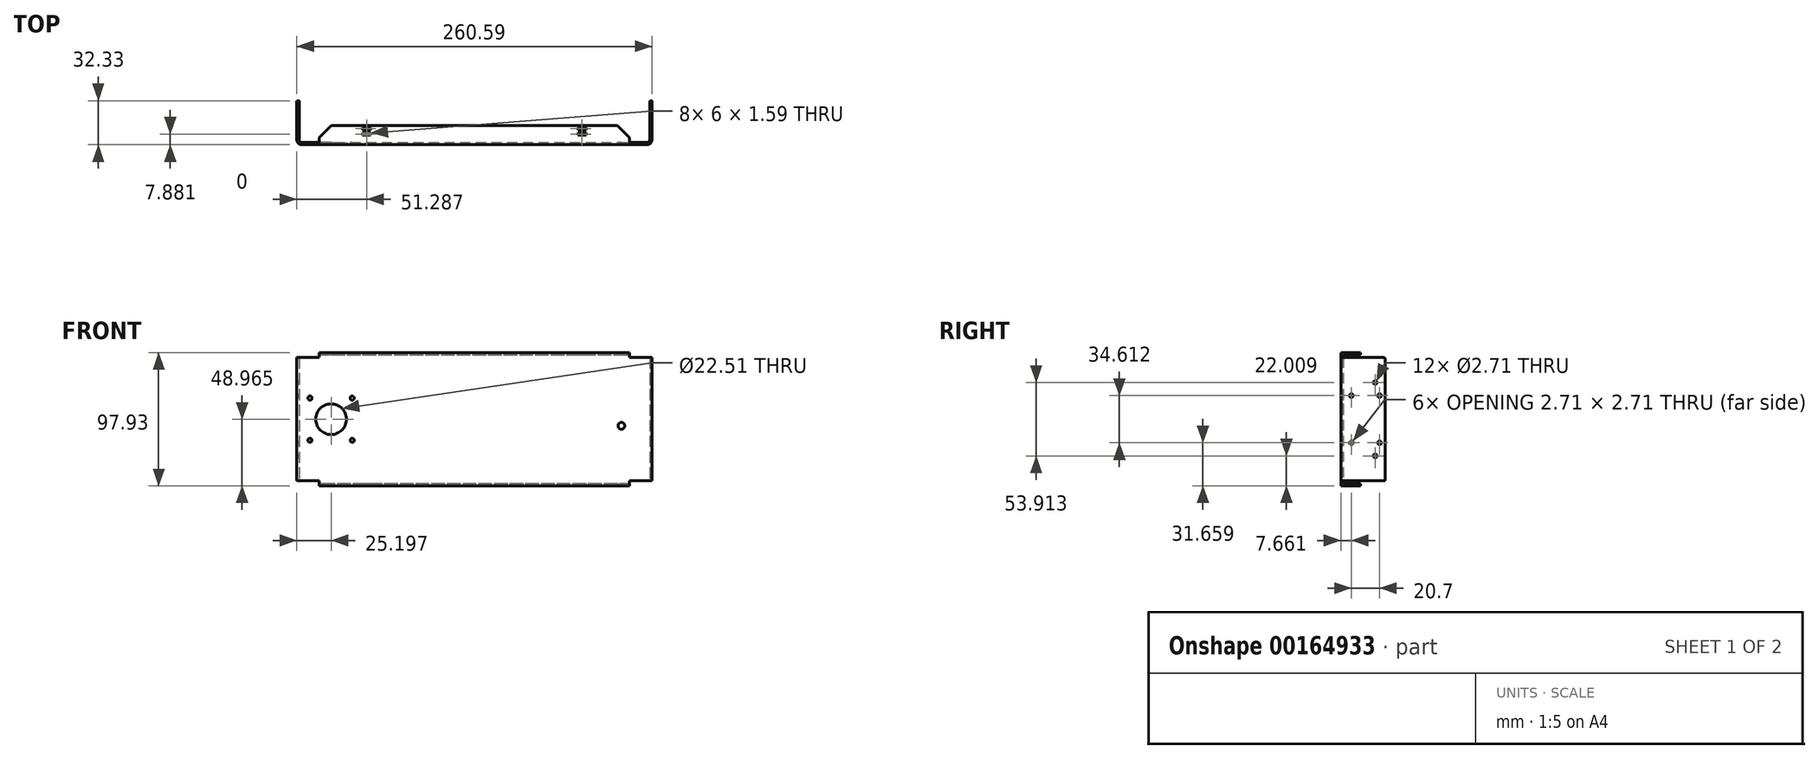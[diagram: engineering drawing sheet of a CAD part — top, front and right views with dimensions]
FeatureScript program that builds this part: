
annotation { "Feature Type Name" : "Feature", "Feature Type Description" : "" }
export const myFeature = defineFeature(function(context is Context, id is Id, definition is map)
    precondition{}
    {
        {
            var Q0;
            Q0=qCreatedBy(makeId("Top.planeOp"),FACE);
            var sketch = newSketch(context, id + "F0", { "sketchPlane" : qUnion([Q0])});
            skLineSegment(sketch, "E0", {"start": v(0, 0) * mm, "end": v(0, -30.62) * mm});
            skLineSegment(sketch, "E1", {"start": v(-1.7, -32.33) * mm, "end": v(-1.7, 0) * mm});
            skLineSegment(sketch, "E2", {"start": v(257.18, -30.62) * mm, "end": v(257.18, 0) * mm});
            skLineSegment(sketch, "E3", {"start": v(258.88, 0) * mm, "end": v(258.88, -32.33) * mm});
            skLineSegment(sketch, "E4", {"start": v(-1.7, -32.33) * mm, "end": v(258.88, -32.33) * mm});
            skLineSegment(sketch, "E5", {"start": v(0, -30.62) * mm, "end": v(257.18, -30.62) * mm});
            skLineSegment(sketch, "E6", {"start": v(257.18, 0) * mm, "end": v(258.88, 0) * mm});
            skLineSegment(sketch, "E7", {"start": v(0, 0) * mm, "end": v(-1.7, 0) * mm});
            skLineSegment(sketch, "E8", {"start": v(128.59, -30.62) * mm, "end": v(128.59, -32.33) * mm, "construction": true});
            skLineSegment(sketch, "E9", {"start": v(258.88, 0) * mm, "end": v(257.18, 0) * mm, "construction": true});
            skSolve(sketch);
        }
        {
            var Q0;
            Q0=qSketchRegion(id+"F0",true);
            extrude(context, id + "F1", {"entities" : qUnion([Q0]), "depth" : 90.55 * mm});
        }
        {
            var Q0;
            Q0=makeQuery(id+"F1.opExtrude","SWEPT_FACE",FACE,{"disambiguationData":[OSD([sQuery(id+"F0.wireOp",EDGE,"E4")])]});
            var sketch = newSketch(context, id + "F2", { "sketchPlane" : qUnion([Q0])});
            skLineSegment(sketch, "E10.bottom", {"start": v(38.99, 60.77) * mm, "end": v(7.99, 60.77) * mm, "construction": true});
            skLineSegment(sketch, "E10.top", {"start": v(38.99, 29.78) * mm, "end": v(7.99, 29.78) * mm, "construction": true});
            skLineSegment(sketch, "E10.left", {"start": v(38.99, 60.77) * mm, "end": v(38.99, 29.78) * mm, "construction": true});
            skLineSegment(sketch, "E10.right", {"start": v(7.99, 60.77) * mm, "end": v(7.99, 29.78) * mm, "construction": true});
            skPoint(sketch, "E10.middle", {"position": v(23.49, 45.28) * mm});
            skCircle(sketch, "E11", {"center": v(23.49, 45.28) * mm, "radius": 11.25 * mm});
            skCircle(sketch, "E12", {"center": v(7.99, 29.78) * mm, "radius": 1.5 * mm});
            skCircle(sketch, "E13", {"center": v(38.99, 29.78) * mm, "radius": 1.5 * mm});
            skCircle(sketch, "E14", {"center": v(38.99, 60.77) * mm, "radius": 1.5 * mm});
            skCircle(sketch, "E15", {"center": v(7.99, 60.77) * mm, "radius": 1.5 * mm});
            skLineSegment(sketch, "E16", {"start": v(23.49, 45.28) * mm, "end": v(-1.7, 45.28) * mm, "construction": true});
            skLineSegment(sketch, "E17", {"start": v(23.49, 45.28) * mm, "end": v(236.47, 45.28) * mm, "construction": true});
            skLineSegment(sketch, "E18", {"start": v(236.47, 40.45) * mm, "end": v(236.47, 45.28) * mm, "construction": true});
            skCircle(sketch, "E19", {"center": v(236.47, 40.45) * mm, "radius": 2.5 * mm});
            skLineSegment(sketch, "E20", {"start": v(236.47, 40.45) * mm, "end": v(258.88, 40.45) * mm, "construction": true});
            skSolve(sketch);
        }
        {
            var Q0;
            Q0 = qSketchRegion(id + "F2", true);
            var Q1;
            Q1=makeQuery(id+"F1.opExtrude","SWEPT_FACE",FACE,{"disambiguationData":[OSD([sQuery(id+"F0.wireOp",EDGE,"E5")])]});
            extrude(context, id + "F3", {"entities" : qUnion([Q0]), "operationType" : NewBodyOperationType.REMOVE, "endBound" : BoundingType.UP_TO_SURFACE, "oppositeDirection" : true, "endBoundEntityFace" : qUnion([Q1]), "depth" : 25.4 * mm});
        }
        {
            var Q0;
            Q0=makeQuery(id+"F1.opExtrude","SWEPT_FACE",FACE,{"disambiguationData":[OSD([sQuery(id+"F0.wireOp",EDGE,"E3")])]});
            var sketch = newSketch(context, id + "F4", { "sketchPlane" : qUnion([Q0])});
            skLineSegment(sketch, "E21", {"start": v(0, 45.28) * mm, "end": v(-7.17, 45.28) * mm, "construction": true});
            skLineSegment(sketch, "E22", {"start": v(-7.17, 18.32) * mm, "end": v(-7.17, 72.23) * mm, "construction": true});
            skCircle(sketch, "E23", {"center": v(-7.17, 18.32) * mm, "radius": 1.35 * mm});
            skCircle(sketch, "E24", {"center": v(-7.17, 72.23) * mm, "radius": 1.35 * mm});
            skLineSegment(sketch, "E25", {"start": v(-7.17, 72.23) * mm, "end": v(-7.17, 90.55) * mm, "construction": true});
            skSolve(sketch);
        }
        {
            var Q0;
            Q0 = qSketchRegion(id + "F4", true);
            var Q1;
            Q1=makeQuery(id+"F1.opExtrude","SWEPT_FACE",FACE,{"disambiguationData":[OSD([sQuery(id+"F0.wireOp",EDGE,"E1")])]});
            extrude(context, id + "F5", {"entities" : qUnion([Q0]), "operationType" : NewBodyOperationType.REMOVE, "endBound" : BoundingType.UP_TO_SURFACE, "oppositeDirection" : true, "endBoundEntityFace" : qUnion([Q1]), "depth" : 25.4 * mm});
        }
        {
            var Q0;
            Q0=makeQuery(id+"F1.opExtrude","CAP_EDGE",EDGE,{"disambiguationData":[OSD([sQuery(id+"F0.wireOp",EDGE,"E6")])],"isStart":false});
            var Q1;
            Q1=makeQuery(id+"F1.opExtrude","CAP_EDGE",EDGE,{"disambiguationData":[OSD([sQuery(id+"F0.wireOp",EDGE,"E6")])],"isStart":true});
            var Q2;
            Q2=makeQuery(id+"F1.opExtrude","CAP_EDGE",EDGE,{"disambiguationData":[OSD([sQuery(id+"F0.wireOp",EDGE,"E7")])],"isStart":false});
            var Q3;
            Q3=makeQuery(id+"F1.opExtrude","CAP_EDGE",EDGE,{"disambiguationData":[OSD([sQuery(id+"F0.wireOp",EDGE,"E7")])],"isStart":true});
            fillet(context, id + "F6", {"entities" : qUnion([Q0, Q1, Q2, Q3]), "radius" : 0.76 * mm, "tangentPropagation" : true, "allowEdgeOverflow" : false});
        }
        {
            var Q0;
            Q0=makeQuery(id+"F1.opExtrude","SWEPT_FACE",FACE,{"disambiguationData":[OSD([sQuery(id+"F0.wireOp",EDGE,"E3")])]});
            var sketch = newSketch(context, id + "F7", { "sketchPlane" : qUnion([Q0])});
            skLineSegment(sketch, "E26", {"start": v(-28.64, 45.28) * mm, "end": v(0, 45.28) * mm, "construction": true});
            skLineSegment(sketch, "E27.bottom", {"start": v(-24.67, 62.58) * mm, "end": v(-3.97, 62.58) * mm, "construction": true});
            skLineSegment(sketch, "E27.top", {"start": v(-24.67, 27.97) * mm, "end": v(-3.97, 27.97) * mm, "construction": true});
            skLineSegment(sketch, "E27.left", {"start": v(-24.67, 62.58) * mm, "end": v(-24.67, 27.97) * mm, "construction": true});
            skLineSegment(sketch, "E27.right", {"start": v(-3.97, 62.58) * mm, "end": v(-3.97, 27.97) * mm, "construction": true});
            skPoint(sketch, "E27.middle", {"position": v(-14.32, 45.28) * mm});
            skLineSegment(sketch, "E28", {"start": v(-24.67, 27.97) * mm, "end": v(-24.67, 0) * mm, "construction": true});
            skLineSegment(sketch, "E29", {"start": v(-24.67, 27.97) * mm, "end": v(-28.64, 27.97) * mm, "construction": true});
            skCircle(sketch, "E30", {"center": v(-24.67, 27.97) * mm, "radius": 1.35 * mm});
            skCircle(sketch, "E31", {"center": v(-3.97, 27.97) * mm, "radius": 1.35 * mm});
            skCircle(sketch, "E32", {"center": v(-3.97, 62.58) * mm, "radius": 1.35 * mm});
            skCircle(sketch, "E33", {"center": v(-24.67, 62.58) * mm, "radius": 1.35 * mm});
            skLineSegment(sketch, "E34", {"start": v(-28.64, 0) * mm, "end": v(-28.64, 90.55) * mm, "construction": true});
            skSolve(sketch);
        }
        {
            var Q0;
            Q0 = qSketchRegion(id + "F7", true);
            var Q1;
            Q1=makeQuery(id+"F1.opExtrude","SWEPT_FACE",FACE,{"disambiguationData":[OSD([sQuery(id+"F0.wireOp",EDGE,"E1")])]});
            extrude(context, id + "F8", {"entities" : qUnion([Q0]), "operationType" : NewBodyOperationType.REMOVE, "endBound" : BoundingType.UP_TO_SURFACE, "oppositeDirection" : true, "endBoundEntityFace" : qUnion([Q1]), "depth" : 25.4 * mm});
        }
        {
            var Q0;
            Q0=makeQuery(id+"F1.opExtrude","SWEPT_FACE",FACE,{"disambiguationData":[OSD([sQuery(id+"F0.wireOp",EDGE,"E5")])]});
            var sketch = newSketch(context, id + "F9", { "sketchPlane" : qUnion([Q0])});
            skLineSegment(sketch, "E35.bottom", {"start": v(-14.68, 0) * mm, "end": v(-242.5, 0) * mm});
            skLineSegment(sketch, "E35.top", {"start": v(-14.68, -3.7) * mm, "end": v(-242.5, -3.7) * mm});
            skLineSegment(sketch, "E35.left", {"start": v(-14.68, 0) * mm, "end": v(-14.68, -3.7) * mm});
            skLineSegment(sketch, "E35.right", {"start": v(-242.5, 0) * mm, "end": v(-242.5, -3.7) * mm});
            skPoint(sketch, "E36", {"position": v(-128.59, 0) * mm});
            skLineSegment(sketch, "E37.bottom", {"start": v(-14.68, 90.55) * mm, "end": v(-242.5, 90.55) * mm});
            skLineSegment(sketch, "E37.top", {"start": v(-14.68, 94.24) * mm, "end": v(-242.5, 94.24) * mm});
            skLineSegment(sketch, "E37.left", {"start": v(-14.68, 90.55) * mm, "end": v(-14.68, 94.24) * mm});
            skLineSegment(sketch, "E37.right", {"start": v(-242.5, 90.55) * mm, "end": v(-242.5, 94.24) * mm});
            skSolve(sketch);
        }
        {
            var Q0;
            Q0 = qSketchRegion(id + "F9", true);
            var Q1;
            Q1=makeQuery(id+"F1.opExtrude","SWEPT_FACE",FACE,{"disambiguationData":[OSD([sQuery(id+"F0.wireOp",EDGE,"E4")])]});
            extrude(context, id + "F10", {"entities" : qUnion([Q0]), "operationType" : NewBodyOperationType.ADD, "endBound" : BoundingType.UP_TO_SURFACE, "oppositeDirection" : true, "endBoundEntityFace" : qUnion([Q1]), "depth" : 25.4 * mm});
        }
        {
            var Q0;
            Q0=makeQuery(id+"F10.boolean.opBoolean","MERGE",FACE,{"derivedFrom":[makeQuery(id+"F1.opExtrude","SWEPT_FACE",FACE,{"disambiguationData":[OSD([sQuery(id+"F0.wireOp",EDGE,"E5")])]}),makeQuery(id+"F10.opExtrude","CAP_FACE",FACE,{"disambiguationData":[OSD([sQuery(id+"F9.wireOp",EDGE,"E35.bottom"),sQuery(id+"F9.wireOp",EDGE,"E35.top"),sQuery(id+"F9.wireOp",EDGE,"E35.left"),sQuery(id+"F9.wireOp",EDGE,"E35.right")])],"isStart":true}),makeQuery(id+"F10.opExtrude","CAP_FACE",FACE,{"disambiguationData":[OSD([sQuery(id+"F9.wireOp",EDGE,"E37.bottom"),sQuery(id+"F9.wireOp",EDGE,"E37.top"),sQuery(id+"F9.wireOp",EDGE,"E37.left"),sQuery(id+"F9.wireOp",EDGE,"E37.right")])],"isStart":true})]});
            var sketch = newSketch(context, id + "F11", { "sketchPlane" : qUnion([Q0])});
            skLineSegment(sketch, "E38.bottom", {"start": v(-14.68, 94.24) * mm, "end": v(-242.5, 94.24) * mm});
            skLineSegment(sketch, "E38.top", {"start": v(-14.68, 92.53) * mm, "end": v(-242.5, 92.53) * mm});
            skLineSegment(sketch, "E38.left", {"start": v(-14.68, 94.24) * mm, "end": v(-14.68, 92.53) * mm});
            skLineSegment(sketch, "E38.right", {"start": v(-242.5, 94.24) * mm, "end": v(-242.5, 92.53) * mm});
            skLineSegment(sketch, "E39.bottom", {"start": v(-242.5, -3.7) * mm, "end": v(-14.68, -3.7) * mm});
            skLineSegment(sketch, "E39.top", {"start": v(-242.5, -1.98) * mm, "end": v(-14.68, -1.98) * mm});
            skLineSegment(sketch, "E39.left", {"start": v(-242.5, -3.7) * mm, "end": v(-242.5, -1.98) * mm});
            skLineSegment(sketch, "E39.right", {"start": v(-14.68, -3.7) * mm, "end": v(-14.68, -1.98) * mm});
            skSolve(sketch);
        }
        {
            var Q0;
            Q0 = qSketchRegion(id + "F11", true);
            extrude(context, id + "F12", {"entities" : qUnion([Q0]), "operationType" : NewBodyOperationType.ADD, "depth" : 12.52 * mm});
        }
        {
            var Q0;
            Q0=makeQuery(id+"F1.opExtrude","SWEPT_EDGE",EDGE,{"disambiguationData":[OSD([sQuery(id+"F0.wireOp",EDGE,"E1"),sQuery(id+"F0.wireOp",EDGE,"E4")])]});
            var Q1;
            Q1=makeQuery(id+"F1.opExtrude","SWEPT_EDGE",EDGE,{"disambiguationData":[OSD([sQuery(id+"F0.wireOp",EDGE,"E3"),sQuery(id+"F0.wireOp",EDGE,"E4")])]});
            var Q2;
            Q2=makeQuery(id+"F10.opExtrude","TWEAK_EDGE",EDGE,{"derivedFrom":[makeQuery(id+"F1.opExtrude","SWEPT_FACE",FACE,{"disambiguationData":[OSD([sQuery(id+"F0.wireOp",EDGE,"E4")])]}),makeQuery(id+"F9.imprint","IMPRINT",EDGE,{"derivedFrom":sQuery(id+"F9.wireOp",EDGE,"E37.top")})]});
            var Q3;
            Q3=makeQuery(id+"F10.opExtrude","TWEAK_EDGE",EDGE,{"derivedFrom":[makeQuery(id+"F1.opExtrude","SWEPT_FACE",FACE,{"disambiguationData":[OSD([sQuery(id+"F0.wireOp",EDGE,"E4")])]}),makeQuery(id+"F9.imprint","IMPRINT",EDGE,{"derivedFrom":sQuery(id+"F9.wireOp",EDGE,"E35.top")})]});
            fillet(context, id + "F13", {"entities" : qUnion([Q0, Q1, Q2, Q3]), "radius" : 3.7 * mm, "tangentPropagation" : true, "allowEdgeOverflow" : false});
        }
        {
            var Q0;
            Q0=makeQuery(id+"F1.opExtrude","SWEPT_EDGE",EDGE,{"disambiguationData":[OSD([sQuery(id+"F0.wireOp",EDGE,"E0"),sQuery(id+"F0.wireOp",EDGE,"E5")])]});
            var Q1;
            Q1=makeQuery(id+"F1.opExtrude","SWEPT_EDGE",EDGE,{"disambiguationData":[OSD([sQuery(id+"F0.wireOp",EDGE,"E2"),sQuery(id+"F0.wireOp",EDGE,"E5")])]});
            var Q2;
            Q2=makeQuery(id+"F12.opExtrude","CAP_EDGE",EDGE,{"disambiguationData":[OSD([sQuery(id+"F11.wireOp",EDGE,"E38.top")])],"isStart":true});
            var Q3;
            Q3=makeQuery(id+"F12.opExtrude","CAP_EDGE",EDGE,{"disambiguationData":[OSD([sQuery(id+"F11.wireOp",EDGE,"E39.top")])],"isStart":true});
            fillet(context, id + "F14", {"entities" : qUnion([Q0, Q1, Q2, Q3]), "radius" : 1.98 * mm, "tangentPropagation" : true, "allowEdgeOverflow" : false});
        }
        {
            var Q0;
            Q0=makeQuery(id+"F12.opExtrude","CAP_EDGE",EDGE,{"disambiguationData":[OSD([sQuery(id+"F11.wireOp",EDGE,"E38.left")])],"isStart":false});
            var Q1;
            Q1=makeQuery(id+"F12.opExtrude","CAP_EDGE",EDGE,{"disambiguationData":[OSD([sQuery(id+"F11.wireOp",EDGE,"E38.right")])],"isStart":false});
            var Q2;
            Q2=makeQuery(id+"F12.opExtrude","CAP_EDGE",EDGE,{"disambiguationData":[OSD([sQuery(id+"F11.wireOp",EDGE,"E39.left")])],"isStart":false});
            var Q3;
            Q3=makeQuery(id+"F12.opExtrude","CAP_EDGE",EDGE,{"disambiguationData":[OSD([sQuery(id+"F11.wireOp",EDGE,"E39.right")])],"isStart":false});
            chamfer(context, id + "F15", {"entities" : qUnion([Q0, Q1, Q2, Q3]), "width" : 8.95 * mm, "tangentPropagation" : true});
        }
        {
            var Q0;
            Q0=makeQuery(id+"F12.boolean.opBoolean","MERGE",FACE,{"derivedFrom":[makeQuery(id+"F10.opExtrude","SWEPT_FACE",FACE,{"disambiguationData":[OSD([sQuery(id+"F9.wireOp",EDGE,"E35.top")])]}),makeQuery(id+"F12.opExtrude","SWEPT_FACE",FACE,{"disambiguationData":[OSD([sQuery(id+"F11.wireOp",EDGE,"E39.bottom")])]})]});
            var sketch = newSketch(context, id + "F16", { "sketchPlane" : qUnion([Q0])});
            skLineSegment(sketch, "E40", {"start": v(23.49, 32.33) * mm, "end": v(23.49, 20.48) * mm, "construction": true});
            skLineSegment(sketch, "E41", {"start": v(23.49, 20.48) * mm, "end": v(46.58, 20.48) * mm, "construction": true});
            skLineSegment(sketch, "E42.bottom", {"start": v(46.58, 21.27) * mm, "end": v(52.58, 21.27) * mm});
            skLineSegment(sketch, "E42.top", {"start": v(46.58, 19.69) * mm, "end": v(52.58, 19.69) * mm});
            skLineSegment(sketch, "E42.left", {"start": v(46.58, 21.27) * mm, "end": v(46.58, 19.69) * mm});
            skLineSegment(sketch, "E42.right", {"start": v(52.58, 21.27) * mm, "end": v(52.58, 19.69) * mm});
            skLineSegment(sketch, "E43", {"start": v(49.58, 19.69) * mm, "end": v(49.58, 18.1) * mm, "construction": true});
            skLineSegment(sketch, "E44.bottom", {"start": v(204.6, 21.27) * mm, "end": v(210.6, 21.27) * mm});
            skLineSegment(sketch, "E44.top", {"start": v(204.6, 19.69) * mm, "end": v(210.6, 19.69) * mm});
            skLineSegment(sketch, "E44.left", {"start": v(204.6, 21.27) * mm, "end": v(204.6, 19.69) * mm});
            skLineSegment(sketch, "E44.right", {"start": v(210.6, 21.27) * mm, "end": v(210.6, 19.69) * mm});
            skLineSegment(sketch, "E45", {"start": v(52.58, 20.48) * mm, "end": v(204.6, 20.48) * mm, "construction": true});
            skLineSegment(sketch, "E46", {"start": v(128.59, 20.48) * mm, "end": v(128.59, 18.1) * mm, "construction": true});
            skLineSegment(sketch, "E47", {"start": v(207.6, 21.27) * mm, "end": v(207.6, 23.66) * mm, "construction": true});
            skLineSegment(sketch, "E48", {"start": v(49.58, 21.27) * mm, "end": v(49.58, 23.66) * mm, "construction": true});
            skLineSegment(sketch, "E49.bottom", {"start": v(46.58, 23.66) * mm, "end": v(52.58, 23.66) * mm});
            skLineSegment(sketch, "E49.top", {"start": v(46.58, 25.24) * mm, "end": v(52.58, 25.24) * mm});
            skLineSegment(sketch, "E49.left", {"start": v(46.58, 23.66) * mm, "end": v(46.58, 25.24) * mm});
            skLineSegment(sketch, "E49.right", {"start": v(52.58, 23.66) * mm, "end": v(52.58, 25.24) * mm});
            skLineSegment(sketch, "E50.bottom", {"start": v(204.6, 23.66) * mm, "end": v(210.6, 23.66) * mm});
            skLineSegment(sketch, "E50.top", {"start": v(204.6, 25.24) * mm, "end": v(210.6, 25.24) * mm});
            skLineSegment(sketch, "E50.left", {"start": v(204.6, 23.66) * mm, "end": v(204.6, 25.24) * mm});
            skLineSegment(sketch, "E50.right", {"start": v(210.6, 23.66) * mm, "end": v(210.6, 25.24) * mm});
            skSolve(sketch);
        }
        {
            var Q0;
            Q0 = qSketchRegion(id + "F16", true);
            var Q1;
            Q1=makeQuery(id+"F12.boolean.opBoolean","MERGE",FACE,{"derivedFrom":[makeQuery(id+"F10.opExtrude","SWEPT_FACE",FACE,{"disambiguationData":[OSD([sQuery(id+"F9.wireOp",EDGE,"E37.top")])]}),makeQuery(id+"F12.opExtrude","SWEPT_FACE",FACE,{"disambiguationData":[OSD([sQuery(id+"F11.wireOp",EDGE,"E38.bottom")])]})]});
            extrude(context, id + "F17", {"entities" : qUnion([Q0]), "operationType" : NewBodyOperationType.REMOVE, "endBound" : BoundingType.UP_TO_SURFACE, "oppositeDirection" : true, "endBoundEntityFace" : qUnion([Q1]), "depth" : 25.4 * mm});
        }
    });
